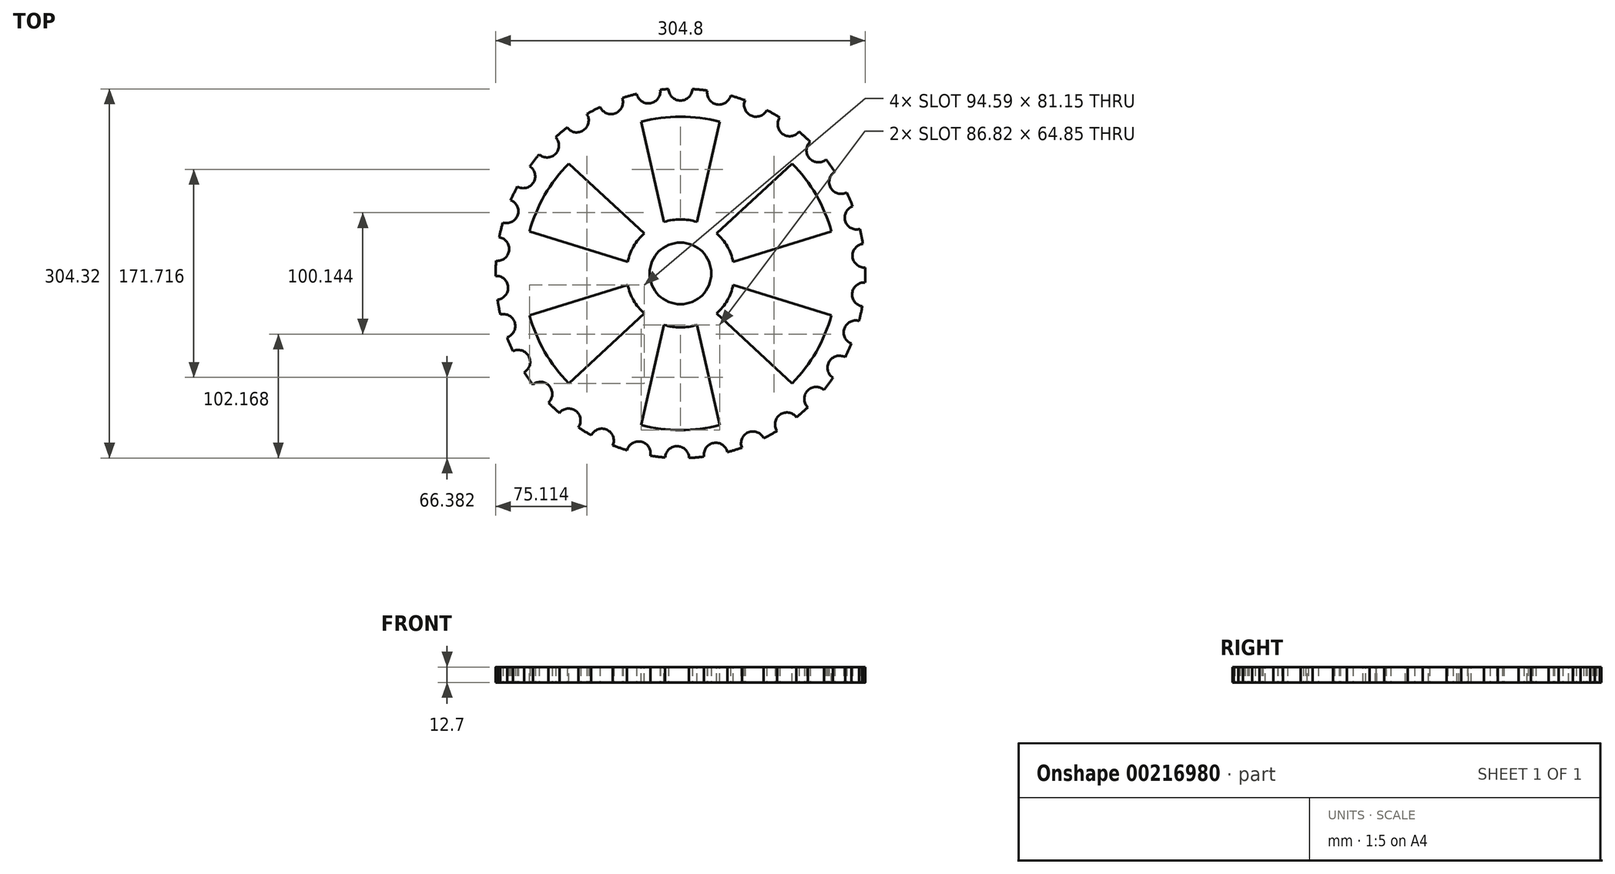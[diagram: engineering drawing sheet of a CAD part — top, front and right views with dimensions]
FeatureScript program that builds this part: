
annotation { "Feature Type Name" : "Feature", "Feature Type Description" : "" }
export const myFeature = defineFeature(function(context is Context, id is Id, definition is map)
    precondition{}
    {
        {
            var Q0;
            Q0=qCreatedBy(makeId("Top.planeOp"),FACE);
            var sketch = newSketch(context, id + "F0", { "sketchPlane" : qUnion([Q0])});
            skCircle(sketch, "E0", {"center": v(0, 0) * mm, "radius": 152.4 * mm});
            skCircle(sketch, "E1", {"center": v(0, 152.4) * mm, "radius": 9.83 * mm});
            skCircle(sketch, "E2.1.0", {"center": v(31.87, 149.03) * mm, "radius": 9.83 * mm});
            skCircle(sketch, "E2.2.0", {"center": v(62.32, 139.07) * mm, "radius": 9.83 * mm});
            skCircle(sketch, "E2.3.0", {"center": v(90.02, 122.97) * mm, "radius": 9.83 * mm});
            skCircle(sketch, "E2.4.0", {"center": v(113.74, 101.43) * mm, "radius": 9.83 * mm});
            skCircle(sketch, "E2.5.0", {"center": v(132.44, 75.4) * mm, "radius": 9.83 * mm});
            skCircle(sketch, "E2.6.0", {"center": v(145.28, 46.05) * mm, "radius": 9.83 * mm});
            skCircle(sketch, "E2.7.0", {"center": v(151.7, 14.65) * mm, "radius": 9.83 * mm});
            skCircle(sketch, "E2.8.0", {"center": v(151.4, -17.39) * mm, "radius": 9.83 * mm});
            skCircle(sketch, "E2.9.0", {"center": v(144.42, -48.66) * mm, "radius": 9.83 * mm});
            skCircle(sketch, "E2.10.0", {"center": v(131.06, -77.78) * mm, "radius": 9.83 * mm});
            skCircle(sketch, "E2.11.0", {"center": v(111.9, -103.47) * mm, "radius": 9.83 * mm});
            skCircle(sketch, "E2.12.0", {"center": v(87.79, -124.58) * mm, "radius": 9.83 * mm});
            skCircle(sketch, "E2.13.0", {"center": v(59.8, -140.18) * mm, "radius": 9.83 * mm});
            skCircle(sketch, "E2.14.0", {"center": v(29.17, -149.58) * mm, "radius": 9.83 * mm});
            skCircle(sketch, "E2.15.0", {"center": v(-2.75, -152.38) * mm, "radius": 9.83 * mm});
            skCircle(sketch, "E2.16.0", {"center": v(-34.55, -148.43) * mm, "radius": 9.83 * mm});
            skCircle(sketch, "E2.17.0", {"center": v(-64.82, -137.93) * mm, "radius": 9.83 * mm});
            skCircle(sketch, "E2.18.0", {"center": v(-92.23, -121.32) * mm, "radius": 9.83 * mm});
            skCircle(sketch, "E2.19.0", {"center": v(-115.56, -99.36) * mm, "radius": 9.83 * mm});
            skCircle(sketch, "E2.20.0", {"center": v(-133.78, -73) * mm, "radius": 9.83 * mm});
            skCircle(sketch, "E2.21.0", {"center": v(-146.08, -43.42) * mm, "radius": 9.83 * mm});
            skCircle(sketch, "E2.22.0", {"center": v(-151.93, -11.91) * mm, "radius": 9.83 * mm});
            skCircle(sketch, "E2.23.0", {"center": v(-151.07, 20.12) * mm, "radius": 9.83 * mm});
            skCircle(sketch, "E2.24.0", {"center": v(-143.52, 51.26) * mm, "radius": 9.83 * mm});
            skCircle(sketch, "E2.25.0", {"center": v(-129.63, 80.14) * mm, "radius": 9.83 * mm});
            skCircle(sketch, "E2.26.0", {"center": v(-110, 105.47) * mm, "radius": 9.83 * mm});
            skCircle(sketch, "E2.27.0", {"center": v(-85.52, 126.14) * mm, "radius": 9.83 * mm});
            skCircle(sketch, "E2.28.0", {"center": v(-57.26, 141.23) * mm, "radius": 9.83 * mm});
            skCircle(sketch, "E2.29.0", {"center": v(-26.46, 150.08) * mm, "radius": 9.83 * mm});
            skLineSegment(sketch, "E2.anchor1", {"start": v(0, 0) * mm, "end": v(0, 152.4) * mm, "construction": true});
            skLineSegment(sketch, "E2.anchor2", {"start": v(0, 0) * mm, "end": v(-26.46, 150.08) * mm, "construction": true});
            skCircle(sketch, "E3", {"center": v(0, 0) * mm, "radius": 25.4 * mm});
            skSolve(sketch);
        }
        {
            var Q0;
            {var subQ1=sQuery(id+"F0.wireOp",EDGE,"E0");var subQ14=sQuery(id+"F0.wireOp",EDGE,"E2.7.0");var subQ15=makeQuery(id+"F0.imprint","INTERSECT",VERTEX,{"disambiguationData":[OD(0.0)],"derivedFrom":[subQ1,subQ14]});Q0=makeQuery(id+"F0.imprint","IMPRINT",FACE,{"disambiguationData":[TD([[makeQuery(id+"F0.imprint","IMPRINT",EDGE,{"disambiguationData":[TD([[subQ15,-1.0]])],"derivedFrom":subQ1}),1.0]])]});}
            extrude(context, id + "F1", {"entities" : qUnion([Q0]), "depth" : 12.7 * mm});
        }
        {
            var Q0;
            Q0=makeQuery(id+"F1.opExtrude","CAP_FACE",FACE,{"disambiguationData":[OSD([sQuery(id+"F0.wireOp",EDGE,"E0"),sQuery(id+"F0.wireOp",EDGE,"E1"),sQuery(id+"F0.wireOp",EDGE,"E2.1.0"),sQuery(id+"F0.wireOp",EDGE,"E2.2.0"),sQuery(id+"F0.wireOp",EDGE,"E2.3.0"),sQuery(id+"F0.wireOp",EDGE,"E2.4.0"),sQuery(id+"F0.wireOp",EDGE,"E2.5.0"),sQuery(id+"F0.wireOp",EDGE,"E2.6.0"),sQuery(id+"F0.wireOp",EDGE,"E2.7.0"),sQuery(id+"F0.wireOp",EDGE,"E2.8.0"),sQuery(id+"F0.wireOp",EDGE,"E2.9.0"),sQuery(id+"F0.wireOp",EDGE,"E2.10.0"),sQuery(id+"F0.wireOp",EDGE,"E2.11.0"),sQuery(id+"F0.wireOp",EDGE,"E2.12.0"),sQuery(id+"F0.wireOp",EDGE,"E2.13.0"),sQuery(id+"F0.wireOp",EDGE,"E2.14.0"),sQuery(id+"F0.wireOp",EDGE,"E2.15.0"),sQuery(id+"F0.wireOp",EDGE,"E2.16.0"),sQuery(id+"F0.wireOp",EDGE,"E2.17.0"),sQuery(id+"F0.wireOp",EDGE,"E2.18.0"),sQuery(id+"F0.wireOp",EDGE,"E2.19.0"),sQuery(id+"F0.wireOp",EDGE,"E2.20.0"),sQuery(id+"F0.wireOp",EDGE,"E2.21.0"),sQuery(id+"F0.wireOp",EDGE,"E2.22.0"),sQuery(id+"F0.wireOp",EDGE,"E2.23.0"),sQuery(id+"F0.wireOp",EDGE,"E2.24.0"),sQuery(id+"F0.wireOp",EDGE,"E2.25.0"),sQuery(id+"F0.wireOp",EDGE,"E2.26.0"),sQuery(id+"F0.wireOp",EDGE,"E2.27.0"),sQuery(id+"F0.wireOp",EDGE,"E2.28.0"),sQuery(id+"F0.wireOp",EDGE,"E2.29.0"),sQuery(id+"F0.wireOp",EDGE,"E3")])],"isStart":false});
            var sketch = newSketch(context, id + "F2", { "sketchPlane" : qUnion([Q0])});
            skCircle(sketch, "E4", {"center": v(0, 0) * mm, "radius": 152.4 * mm, "construction": true});
            skLineSegment(sketch, "E5", {"start": v(0, 0) * mm, "end": v(0, 152.4) * mm, "construction": true});
            skArc(sketch, "E6", {"start": v(32.42, 125.14) * mm, "mid": v(0, 129.27) * mm, "end": v(-32.42, 125.14) * mm});
            skArc(sketch, "E7", {"start": v(13.54, 42.45) * mm, "mid": v(0, 44.55) * mm, "end": v(-13.54, 42.45) * mm});
            skLineSegment(sketch, "E8", {"start": v(-13.54, 42.45) * mm, "end": v(-32.42, 125.14) * mm});
            skLineSegment(sketch, "E9.MirrorCS", {"start": v(13.54, 42.45) * mm, "end": v(32.42, 125.14) * mm});
            skLineSegment(sketch, "E10.1.0", {"start": v(-29.99, 32.95) * mm, "end": v(-92.16, 90.65) * mm});
            skArc(sketch, "E10.1.1", {"start": v(-92.16, 90.65) * mm, "mid": v(-111.95, 64.63) * mm, "end": v(-124.58, 34.49) * mm});
            skArc(sketch, "E10.1.2", {"start": v(-29.99, 32.95) * mm, "mid": v(-38.59, 22.28) * mm, "end": v(-43.53, 9.5) * mm});
            skLineSegment(sketch, "E10.1.3", {"start": v(-43.53, 9.5) * mm, "end": v(-124.58, 34.49) * mm});
            skLineSegment(sketch, "E10.2.0", {"start": v(-43.53, -9.5) * mm, "end": v(-124.58, -34.49) * mm});
            skArc(sketch, "E10.2.1", {"start": v(-124.58, -34.49) * mm, "mid": v(-111.95, -64.63) * mm, "end": v(-92.16, -90.65) * mm});
            skArc(sketch, "E10.2.2", {"start": v(-43.53, -9.5) * mm, "mid": v(-38.59, -22.28) * mm, "end": v(-29.99, -32.95) * mm});
            skLineSegment(sketch, "E10.2.3", {"start": v(-29.99, -32.95) * mm, "end": v(-92.16, -90.65) * mm});
            skLineSegment(sketch, "E10.3.0", {"start": v(-13.54, -42.45) * mm, "end": v(-32.42, -125.14) * mm});
            skArc(sketch, "E10.3.1", {"start": v(-32.42, -125.14) * mm, "mid": v(0, -129.27) * mm, "end": v(32.42, -125.14) * mm});
            skArc(sketch, "E10.3.2", {"start": v(-13.54, -42.45) * mm, "mid": v(0, -44.55) * mm, "end": v(13.54, -42.45) * mm});
            skLineSegment(sketch, "E10.3.3", {"start": v(13.54, -42.45) * mm, "end": v(32.42, -125.14) * mm});
            skLineSegment(sketch, "E10.4.0", {"start": v(29.99, -32.95) * mm, "end": v(92.16, -90.65) * mm});
            skArc(sketch, "E10.4.1", {"start": v(92.16, -90.65) * mm, "mid": v(111.95, -64.63) * mm, "end": v(124.58, -34.49) * mm});
            skArc(sketch, "E10.4.2", {"start": v(29.99, -32.95) * mm, "mid": v(38.59, -22.28) * mm, "end": v(43.53, -9.5) * mm});
            skLineSegment(sketch, "E10.4.3", {"start": v(43.53, -9.5) * mm, "end": v(124.58, -34.49) * mm});
            skLineSegment(sketch, "E10.5.0", {"start": v(43.53, 9.5) * mm, "end": v(124.58, 34.49) * mm});
            skArc(sketch, "E10.5.1", {"start": v(124.58, 34.49) * mm, "mid": v(111.95, 64.63) * mm, "end": v(92.16, 90.65) * mm});
            skArc(sketch, "E10.5.2", {"start": v(43.53, 9.5) * mm, "mid": v(38.59, 22.28) * mm, "end": v(29.99, 32.95) * mm});
            skLineSegment(sketch, "E10.5.3", {"start": v(29.99, 32.95) * mm, "end": v(92.16, 90.65) * mm});
            skSolve(sketch);
        }
        {
            var Q0;
            Q0=makeQuery(id+"F2.imprint","IMPRINT",FACE,{"disambiguationData":[TD([[makeQuery(id+"F2.imprint","IMPRINT",EDGE,{"derivedFrom":sQuery(id+"F2.wireOp",EDGE,"E10.1.0")}),1.0]])]});
            var Q1;
            Q1=makeQuery(id+"F2.imprint","IMPRINT",FACE,{"disambiguationData":[TD([[makeQuery(id+"F2.imprint","IMPRINT",EDGE,{"derivedFrom":sQuery(id+"F2.wireOp",EDGE,"E6")}),1.0]])]});
            var Q2;
            Q2=makeQuery(id+"F2.imprint","IMPRINT",FACE,{"disambiguationData":[TD([[makeQuery(id+"F2.imprint","IMPRINT",EDGE,{"derivedFrom":sQuery(id+"F2.wireOp",EDGE,"E10.5.0")}),1.0]])]});
            var Q3;
            Q3=makeQuery(id+"F2.imprint","IMPRINT",FACE,{"disambiguationData":[TD([[makeQuery(id+"F2.imprint","IMPRINT",EDGE,{"derivedFrom":sQuery(id+"F2.wireOp",EDGE,"E10.4.0")}),1.0]])]});
            var Q4;
            Q4=makeQuery(id+"F2.imprint","IMPRINT",FACE,{"disambiguationData":[TD([[makeQuery(id+"F2.imprint","IMPRINT",EDGE,{"derivedFrom":sQuery(id+"F2.wireOp",EDGE,"E10.3.0")}),1.0]])]});
            var Q5;
            Q5=makeQuery(id+"F2.imprint","IMPRINT",FACE,{"disambiguationData":[TD([[makeQuery(id+"F2.imprint","IMPRINT",EDGE,{"derivedFrom":sQuery(id+"F2.wireOp",EDGE,"E10.2.0")}),1.0]])]});
            extrude(context, id + "F3", {"entities" : qUnion([Q0, Q1, Q2, Q3, Q4, Q5]), "operationType" : NewBodyOperationType.REMOVE, "oppositeDirection" : true, "depth" : 25.4 * mm});
        }
    });
